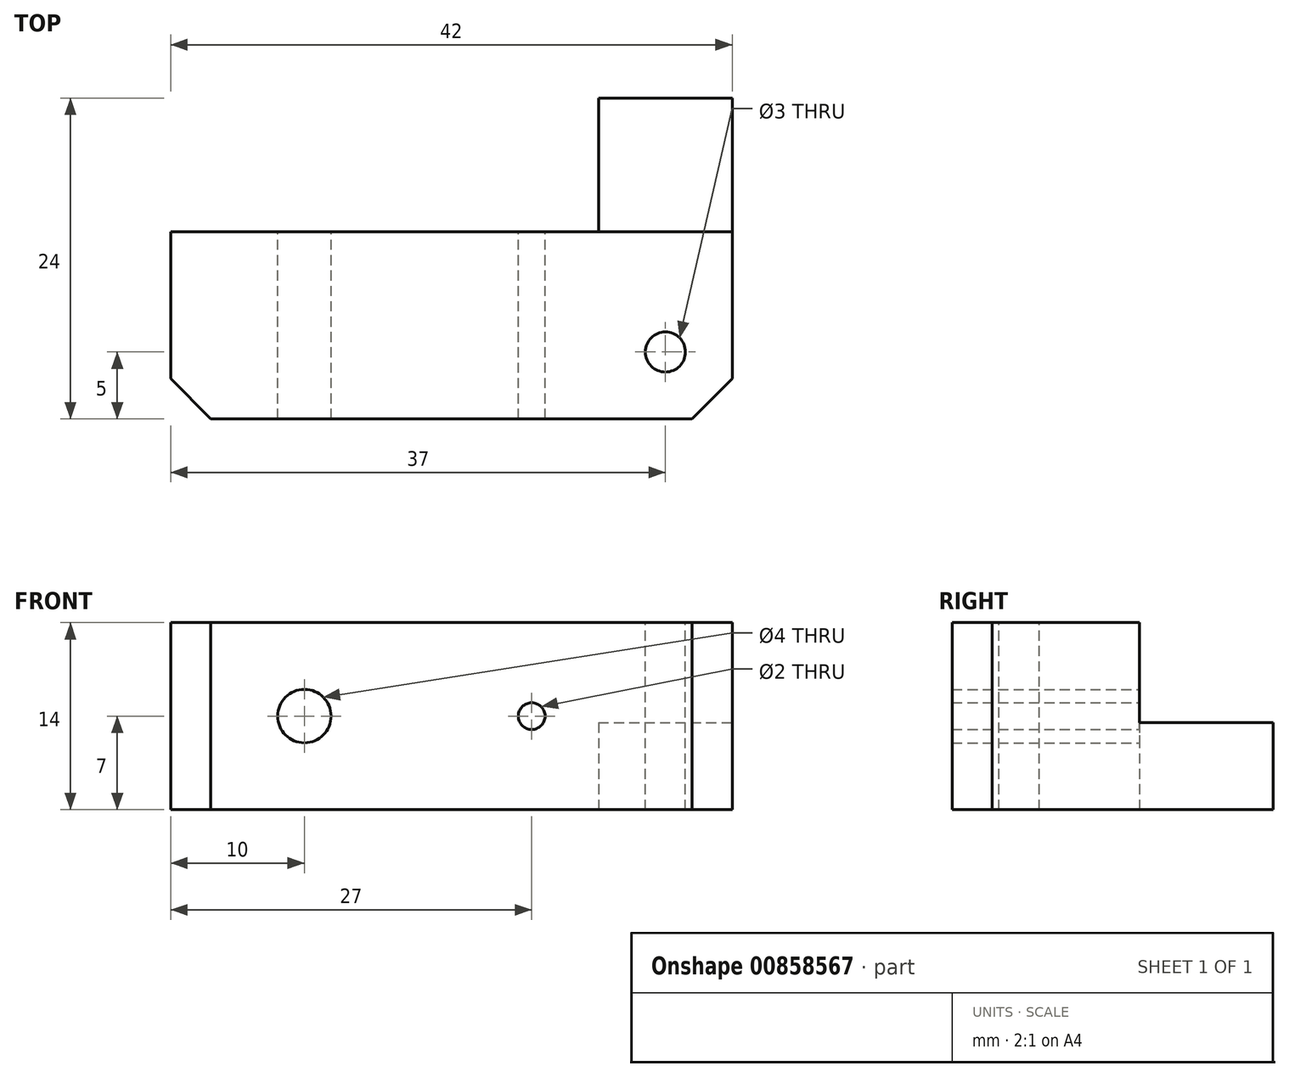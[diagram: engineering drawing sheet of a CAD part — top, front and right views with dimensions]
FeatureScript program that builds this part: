
annotation { "Feature Type Name" : "Feature", "Feature Type Description" : "" }
export const myFeature = defineFeature(function(context is Context, id is Id, definition is map)
    precondition{}
    {
        {
            var Q0;
            Q0=qCreatedBy(makeId("Top.planeOp"),FACE);
            var sketch = newSketch(context, id + "F0", { "sketchPlane" : qUnion([Q0])});
            skLineSegment(sketch, "E0.bottom", {"start": v(0, 0) * mm, "end": v(42, 0) * mm});
            skLineSegment(sketch, "E0.top", {"start": v(0, -14) * mm, "end": v(42, -14) * mm});
            skLineSegment(sketch, "E0.left", {"start": v(0, 0) * mm, "end": v(0, -14) * mm});
            skLineSegment(sketch, "E0.right", {"start": v(42, 0) * mm, "end": v(42, -14) * mm});
            skSolve(sketch);
        }
        {
            var Q0;
            Q0=makeQuery(id+"F0.imprint","IMPRINT",FACE,{"disambiguationData":[TD([[makeQuery(id+"F0.imprint","IMPRINT",EDGE,{"derivedFrom":sQuery(id+"F0.wireOp",EDGE,"E0.bottom")}),-1.0]])]});
            extrude(context, id + "F1", {"entities" : qUnion([Q0]), "depth" : 14 * mm, "offsetDistance" : 25 * mm});
        }
        {
            var Q0;
            Q0=makeQuery(id+"F1.opExtrude","CAP_FACE",FACE,{"disambiguationData":[OSD([sQuery(id+"F0.wireOp",EDGE,"E0.bottom"),sQuery(id+"F0.wireOp",EDGE,"E0.top"),sQuery(id+"F0.wireOp",EDGE,"E0.left"),sQuery(id+"F0.wireOp",EDGE,"E0.right")])],"isStart":false});
            var sketch = newSketch(context, id + "F2", { "sketchPlane" : qUnion([Q0])});
            skLineSegment(sketch, "E1", {"start": v(0, -14) * mm, "end": v(5, -14) * mm});
            skLineSegment(sketch, "E2", {"start": v(5, -14) * mm, "end": v(5, -9) * mm});
            skLineSegment(sketch, "E3", {"start": v(42, -14) * mm, "end": v(37, -14) * mm});
            skLineSegment(sketch, "E4", {"start": v(37, -14) * mm, "end": v(37, -9) * mm});
            skCircle(sketch, "E5", {"center": v(37, -9) * mm, "radius": 1.5 * mm});
            skSolve(sketch);
        }
        {
            var Q0;
            Q0=qSketchRegion(id+"F2",true);
            extrude(context, id + "F3", {"entities" : qUnion([Q0]), "operationType" : NewBodyOperationType.REMOVE, "oppositeDirection" : true, "depth" : 25 * mm, "offsetDistance" : 25 * mm});
        }
        {
            var Q0;
            Q0=makeQuery(id+"F1.opExtrude","SWEPT_EDGE",EDGE,{"disambiguationData":[OSD([sQuery(id+"F0.wireOp",EDGE,"E0.top"),sQuery(id+"F0.wireOp",EDGE,"E0.left")])]});
            var Q1;
            Q1=makeQuery(id+"F1.opExtrude","SWEPT_EDGE",EDGE,{"disambiguationData":[OSD([sQuery(id+"F0.wireOp",EDGE,"E0.top"),sQuery(id+"F0.wireOp",EDGE,"E0.right")])]});
            chamfer(context, id + "F4", {"entities" : qUnion([Q0, Q1]), "width" : 3 * mm, "tangentPropagation" : true});
        }
        {
            var Q0;
            Q0=makeQuery(id+"F1.opExtrude","SWEPT_FACE",FACE,{"disambiguationData":[OSD([sQuery(id+"F0.wireOp",EDGE,"E0.bottom")])]});
            var sketch = newSketch(context, id + "F5", { "sketchPlane" : qUnion([Q0])});
            skLineSegment(sketch, "E6", {"start": v(-42, 7) * mm, "end": v(-27, 7) * mm});
            skCircle(sketch, "E7", {"center": v(-27, 7) * mm, "radius": 1 * mm});
            skLineSegment(sketch, "E8", {"start": v(0, 7) * mm, "end": v(-10, 7) * mm});
            skCircle(sketch, "E9", {"center": v(-10, 7) * mm, "radius": 2 * mm});
            skSolve(sketch);
        }
        {
            var Q0;
            Q0 = qSketchRegion(id + "F5", true);
            extrude(context, id + "F6", {"entities" : qUnion([Q0]), "operationType" : NewBodyOperationType.REMOVE, "oppositeDirection" : true, "depth" : 25 * mm, "offsetDistance" : 25 * mm});
        }
        {
            var Q0;
            Q0 = qSketchRegion(id + "F5", true);
            extrude(context, id + "F7", {"entities" : qUnion([Q0]), "operationType" : NewBodyOperationType.REMOVE, "oppositeDirection" : true, "depth" : 25 * mm, "offsetDistance" : 25 * mm});
        }
        {
            var Q0;
            Q0=makeQuery(id+"F1.opExtrude","SWEPT_FACE",FACE,{"disambiguationData":[OSD([sQuery(id+"F0.wireOp",EDGE,"E0.bottom")])]});
            var sketch = newSketch(context, id + "F8", { "sketchPlane" : qUnion([Q0])});
            skLineSegment(sketch, "E10.bottom", {"start": v(-42, 14) * mm, "end": v(-32, 14) * mm});
            skLineSegment(sketch, "E10.top", {"start": v(-42, 0) * mm, "end": v(-32, 0) * mm});
            skLineSegment(sketch, "E10.left", {"start": v(-42, 14) * mm, "end": v(-42, 0) * mm});
            skLineSegment(sketch, "E10.right", {"start": v(-32, 14) * mm, "end": v(-32, 0) * mm});
            skSolve(sketch);
        }
        {
            var Q0;
            Q0 = qSketchRegion(id + "F8", true);
            extrude(context, id + "F9", {"entities" : qUnion([Q0]), "operationType" : NewBodyOperationType.ADD, "depth" : 10 * mm, "offsetDistance" : 25 * mm});
        }
        {
            var Q0;
            Q0=makeQuery(id+"F9.boolean.opBoolean","MERGE",FACE,{"derivedFrom":[makeQuery(id+"F1.opExtrude","CAP_FACE",FACE,{"disambiguationData":[OSD([sQuery(id+"F0.wireOp",EDGE,"E0.bottom"),sQuery(id+"F0.wireOp",EDGE,"E0.top"),sQuery(id+"F0.wireOp",EDGE,"E0.left"),sQuery(id+"F0.wireOp",EDGE,"E0.right")])],"isStart":false}),makeQuery(id+"F9.opExtrude","SWEPT_FACE",FACE,{"disambiguationData":[OSD([sQuery(id+"F8.wireOp",EDGE,"E10.bottom")])]})]});
            var sketch = newSketch(context, id + "F10", { "sketchPlane" : qUnion([Q0])});
            skLineSegment(sketch, "E11.bottom", {"start": v(42, 10) * mm, "end": v(32, 10) * mm});
            skLineSegment(sketch, "E11.top", {"start": v(42, 0) * mm, "end": v(32, 0) * mm});
            skLineSegment(sketch, "E11.left", {"start": v(42, 10) * mm, "end": v(42, 0) * mm});
            skLineSegment(sketch, "E11.right", {"start": v(32, 10) * mm, "end": v(32, 0) * mm});
            skSolve(sketch);
        }
        {
            var Q0;
            Q0 = qSketchRegion(id + "F10", true);
            extrude(context, id + "F11", {"entities" : qUnion([Q0]), "operationType" : NewBodyOperationType.REMOVE, "oppositeDirection" : true, "depth" : 7.5 * mm, "offsetDistance" : 25 * mm});
        }
    });
